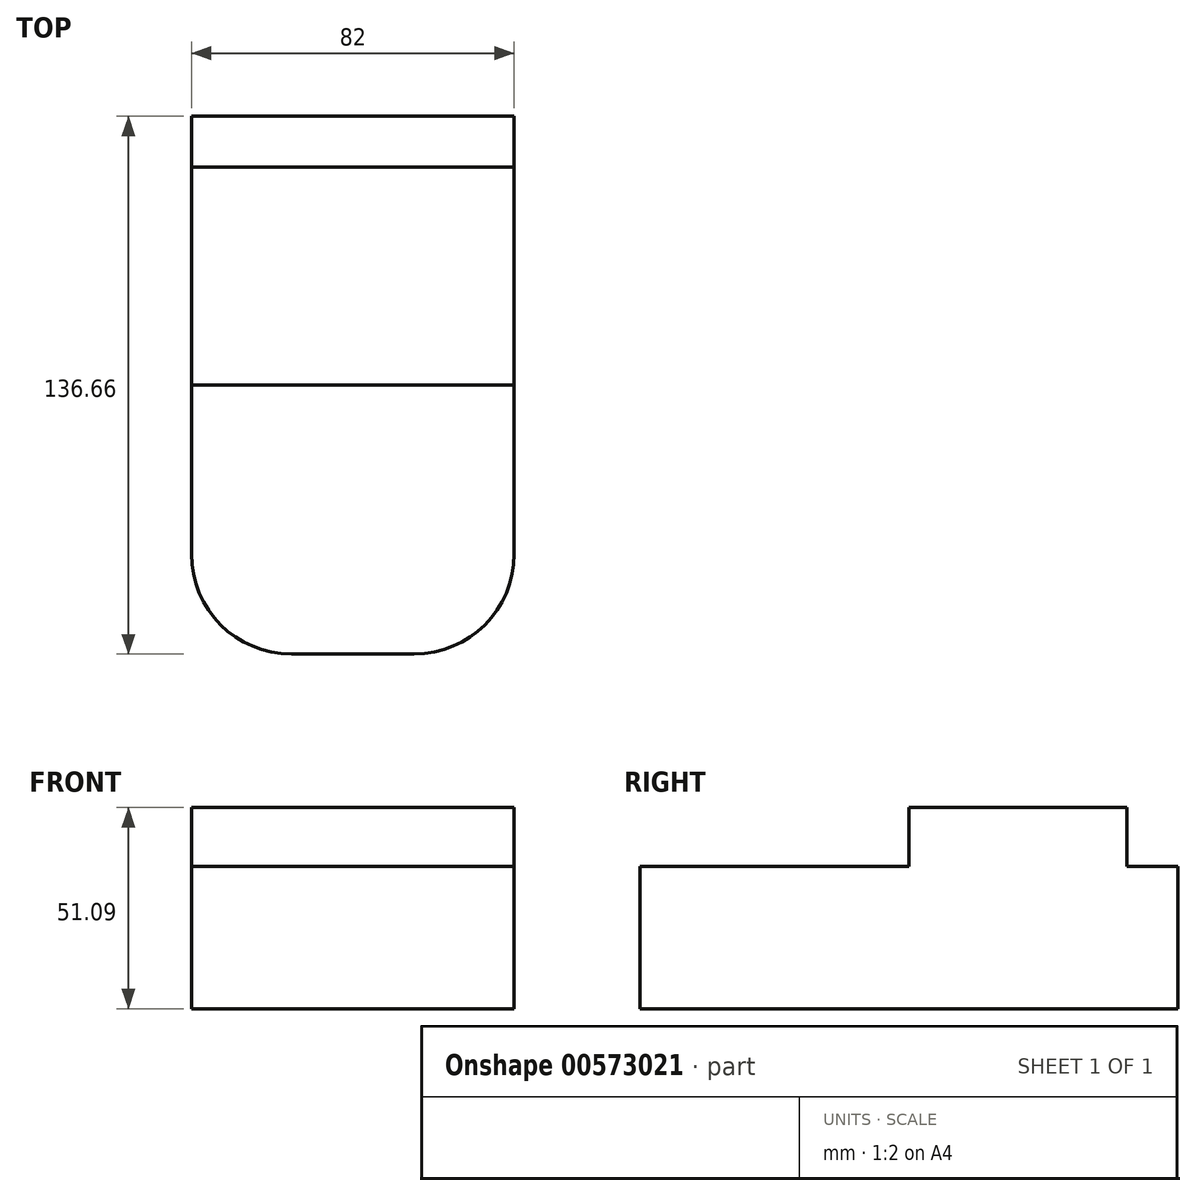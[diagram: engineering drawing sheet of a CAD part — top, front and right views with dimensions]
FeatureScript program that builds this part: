
annotation { "Feature Type Name" : "Feature", "Feature Type Description" : "" }
export const myFeature = defineFeature(function(context is Context, id is Id, definition is map)
    precondition{}
    {
        {
            var Q0;
            Q0=qCreatedBy(makeId("Top.planeOp"),FACE);
            var sketch = newSketch(context, id + "F0", { "sketchPlane" : qUnion([Q0])});
            skLineSegment(sketch, "E0.bottom", {"start": v(15.6, -68.33) * mm, "end": v(-15.6, -68.33) * mm});
            skLineSegment(sketch, "E0.top", {"start": v(41, 68.33) * mm, "end": v(-41, 68.33) * mm});
            skLineSegment(sketch, "E0.left", {"start": v(41, -42.93) * mm, "end": v(41, 68.33) * mm});
            skLineSegment(sketch, "E0.right", {"start": v(-41, -42.93) * mm, "end": v(-41, 68.33) * mm});
            skPoint(sketch, "E0.middle", {"position": v(0, 0) * mm});
            skPoint(sketch, "E1.visualSharp", {"position": v(-41, -68.33) * mm});
            skArc(sketch, "E1.filletArc", {"start": v(-41, -42.93) * mm, "mid": v(-33.56, -60.89) * mm, "end": v(-15.6, -68.33) * mm});
            skPoint(sketch, "E2.visualSharp", {"position": v(41, -68.33) * mm});
            skArc(sketch, "E2.filletArc", {"start": v(15.6, -68.33) * mm, "mid": v(33.56, -60.89) * mm, "end": v(41, -42.93) * mm});
            skSolve(sketch);
        }
        {
            var Q0;
            Q0 = qSketchRegion(id + "F0", true);
            extrude(context, id + "F1", {"entities" : qUnion([Q0]), "depth" : 36.17 * mm, "offsetDistance" : 25.4 * mm});
        }
        {
            var Q0;
            Q0=makeQuery(id+"F1.opExtrude","CAP_FACE",FACE,{"disambiguationData":[OSD([sQuery(id+"F0.wireOp",EDGE,"E0.bottom"),sQuery(id+"F0.wireOp",EDGE,"E0.top"),sQuery(id+"F0.wireOp",EDGE,"E0.left"),sQuery(id+"F0.wireOp",EDGE,"E0.right"),sQuery(id+"F0.wireOp",EDGE,"E1.filletArc"),sQuery(id+"F0.wireOp",EDGE,"E2.filletArc")])],"isStart":false});
            var sketch = newSketch(context, id + "F2", { "sketchPlane" : qUnion([Q0])});
            skLineSegment(sketch, "E3", {"start": v(-41, 55.35) * mm, "end": v(41, 55.35) * mm});
            skLineSegment(sketch, "E4", {"start": v(-41, 0) * mm, "end": v(41, 0) * mm});
            skLineSegment(sketch, "E5", {"start": v(-41, 0) * mm, "end": v(-41, 55.35) * mm});
            skLineSegment(sketch, "E6", {"start": v(41, 0) * mm, "end": v(41, 55.35) * mm});
            skSolve(sketch);
        }
        {
            var Q0;
            Q0 = qSketchRegion(id + "F2", true);
            extrude(context, id + "F3", {"entities" : qUnion([Q0]), "operationType" : NewBodyOperationType.ADD, "depth" : 14.92 * mm, "offsetDistance" : 25.4 * mm});
        }
    });
